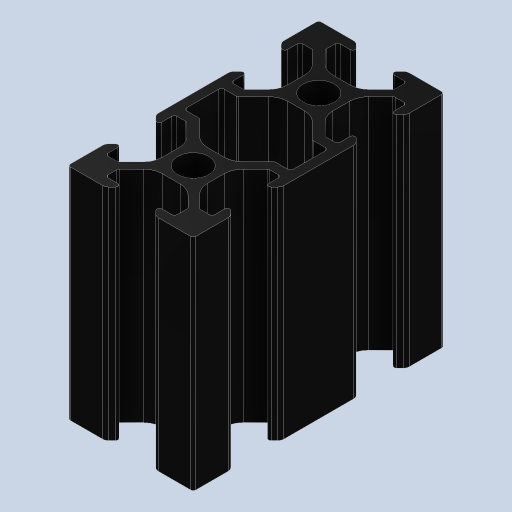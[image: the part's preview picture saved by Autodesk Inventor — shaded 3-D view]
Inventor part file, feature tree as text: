
AUTODESK INVENTOR PART (.ipt)
format: ipt  version: 2023 (Build 270158000, 158)  size: 361,984 bytes
history: native  units: mm
features: other x1, extrude x1, sketch x1
ambient origin geometry x8: Origin, YZ Plane, XZ Plane, XY Plane, X Axis, Y Axis, Z Axis, Center Point
bodies: Body1 (feature_tree)
feature tree (3):
  other  "Sólido1"
  extrude  "Extrusão1"  TaperAngle=45.0deg  [1 undecoded]
  sketch  "Esboço2"  dims[d137=4.5mm d138=45.0deg d139=6.4mm d141=1.5mm d142=1.5mm d145=0.4mm d146=6.5mm d147=45.0deg d148=1.0mm d151=20.0mm d152=20.0mm d153=5.2mm d154=7.4mm d155=13.6mm d156=3.0mm d157=135.0deg d158=3.0mm d159=5.0mm d160=5.0mm d161=0.4mm d162=35.0mm d163=0.0mm]
note: 1 required parameter value undecoded (feature->parameter linkage not recoverable at this tier; creation-order binding heuristic only, values carry confidence <= 0.55)
